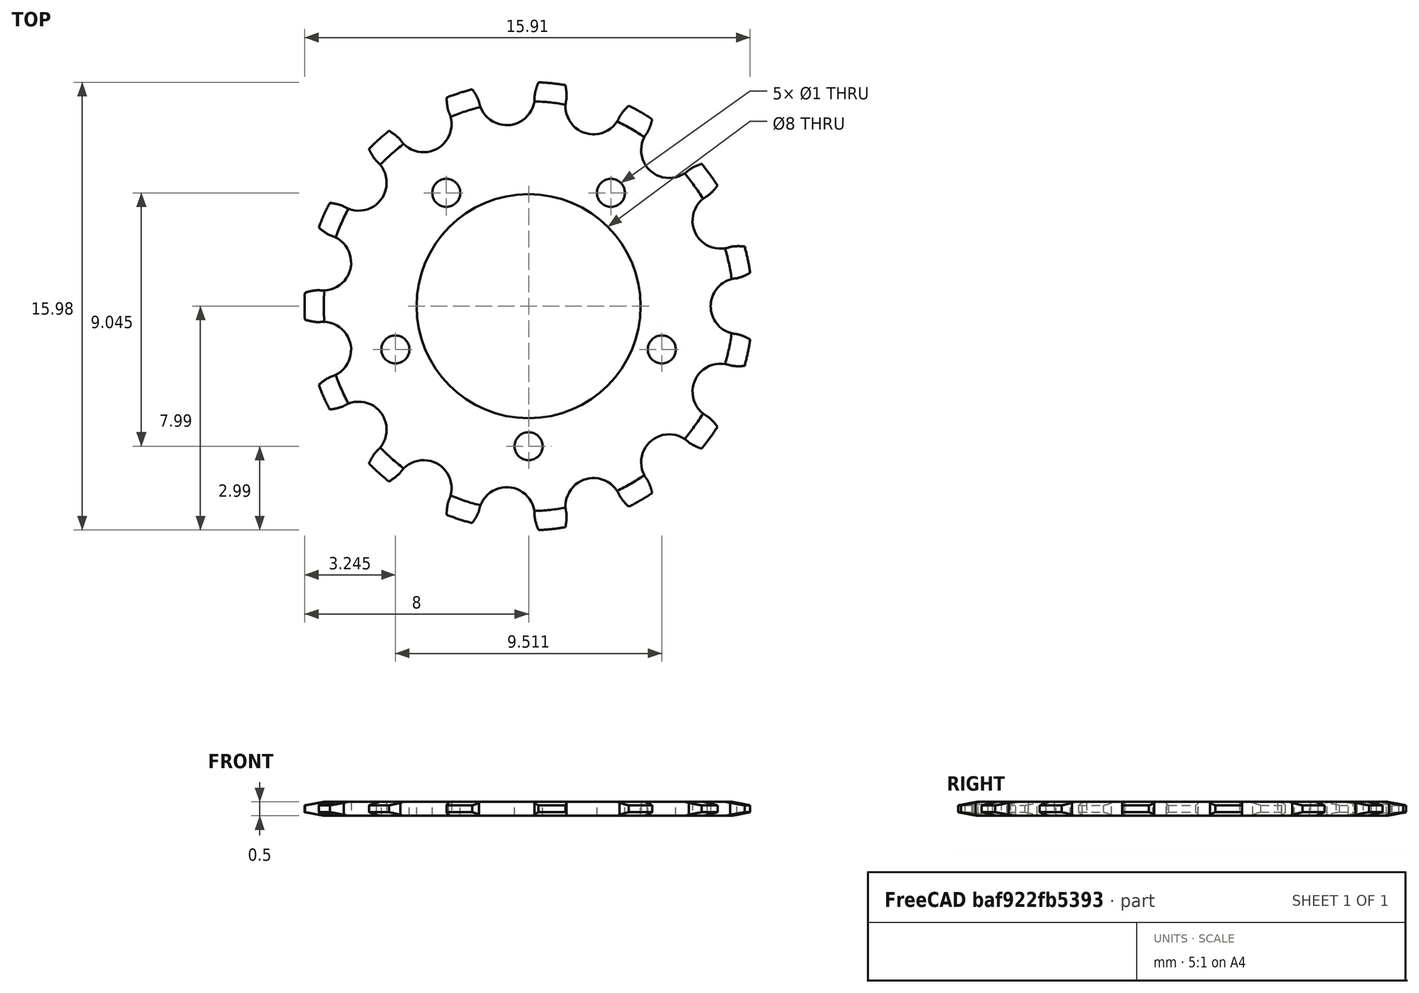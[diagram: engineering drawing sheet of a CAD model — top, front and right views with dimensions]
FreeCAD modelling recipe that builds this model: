
FCSTD DOCUMENT  (FreeCAD 0.19R21938 (Git))
Label: bicycle_chainring
License: All rights reserved
LicenseURL: http://en.wikipedia.org/wiki/All_rights_reserved
objects: Part::Feature×5, Part::Cut×2, Part::FeaturePython×1, Sketcher::SketchObject×1, Part::Revolution×1, Part::MultiCommon×1, Part::Cylinder×1, Part::Compound×1
note: 13 computed .brp shape members not serialized (recipe doc carries the construction recipe); baked Part::Feature solids carry a one-line shape summary decoded from their .brp

FEATURE [Part::FeaturePython] LaternGear  # WARN: FeaturePython — macro-defined, semantics opaque (R4)
  bolt_radius = 1
  height = 0.5
  module = 1
  num_profiles = 10
  teeth = 15
FEATURE [Sketcher::SketchObject] Sketch
  ExternalGeometry = -> [LaternGear]
  Placement = pos=(0,0,0) rot=(-1,0,0;4.71239rad)
  sketch-geometry (7):
    g0: LineSegment StartX=-7.31178 StartY=0.5 StartZ=0 EndX=0 EndY=0.5 EndZ=0
    g1: LineSegment StartX=0 StartY=0.5 StartZ=0 EndX=0 EndY=0 EndZ=0
    g2: LineSegment StartX=0 StartY=0 StartZ=0 EndX=-7.31178 EndY=0 EndZ=0
    g3: LineSegment StartX=-8.11104 StartY=0.35103 StartZ=0 EndX=-8.11104 EndY=0.14897 EndZ=0
    g4: LineSegment [constr] StartX=-8.2833 StartY=0.25 StartZ=0 EndX=7.00346 EndY=0.25 EndZ=0
    g5: LineSegment StartX=-8.11104 StartY=0.35103 StartZ=0 EndX=-7.31178 EndY=0.5 EndZ=0
    g6: LineSegment StartX=-8.11104 StartY=0.14897 StartZ=0 EndX=-7.31178 EndY=0 EndZ=0
  constraints (13):
    c: Coincident(g0,g1)
    c: Coincident(g1,g2)
    c: Horizontal(g0)
    c: Horizontal(g2)
    c: Vertical(g1)
    c: Coincident(g1,g-1)
    c: Symmetric(g-3,g-3,g4)
    c: Symmetric(g2,g0,g4)
    c: Coincident(g5,g3)
    c: Coincident(g5,g0)
    c: Coincident(g6,g3)
    c: Coincident(g6,g2)
    c: Symmetric(g3,g3,g4)
FEATURE [Part::Revolution] Revolve
  Angle = 360
  Axis = (0,0,1)
  Base = (0,0,0)
  FaceMakerClass = Part::FaceMakerBullseye
  Solid = true
  Source = -> Sketch
  Symmetric = false
FEATURE [Part::MultiCommon] Common
  Shapes = -> [LaternGear,Revolve]
FEATURE [Part::Cylinder] Cylinder
  Angle = 360
  AttacherType = Attacher::AttachEngine3D
  Height = 10
  Radius = 4
FEATURE [Part::Cut] Cut
  Base = -> Common
  Tool = -> Cylinder
FEATURE [Part::Feature] Solid
  Placement = pos=(0,-5,-3) rot=(0,0,1;0rad)
  shape: bbox 1 x 1 x 10 mm, 3 faces (baked)
FEATURE [Part::Feature] Solid001
  Placement = pos=(4.75528,-1.54508,-3) rot=(0,0,1;1.25664rad)
  shape: bbox 1 x 1 x 10 mm, 3 faces (baked)
FEATURE [Part::Feature] Solid002
  Placement = pos=(2.93893,4.04508,-3) rot=(0,0,1;2.51327rad)
  shape: bbox 1 x 1 x 10 mm, 3 faces (baked)
FEATURE [Part::Feature] Solid003
  Placement = pos=(-2.93893,4.04508,-3) rot=(0,0,1;3.76991rad)
  shape: bbox 1 x 1 x 10 mm, 3 faces (baked)
FEATURE [Part::Feature] Solid004
  Placement = pos=(-4.75528,-1.54508,-3) rot=(0,0,-1;1.25664rad)
  shape: bbox 1 x 1 x 10 mm, 3 faces (baked)
FEATURE [Part::Compound] Compound
  Links = -> [Solid,Solid001,Solid002,Solid003,Solid004]
FEATURE [Part::Cut] Cut001
  Base = -> Cut
  Tool = -> Compound
